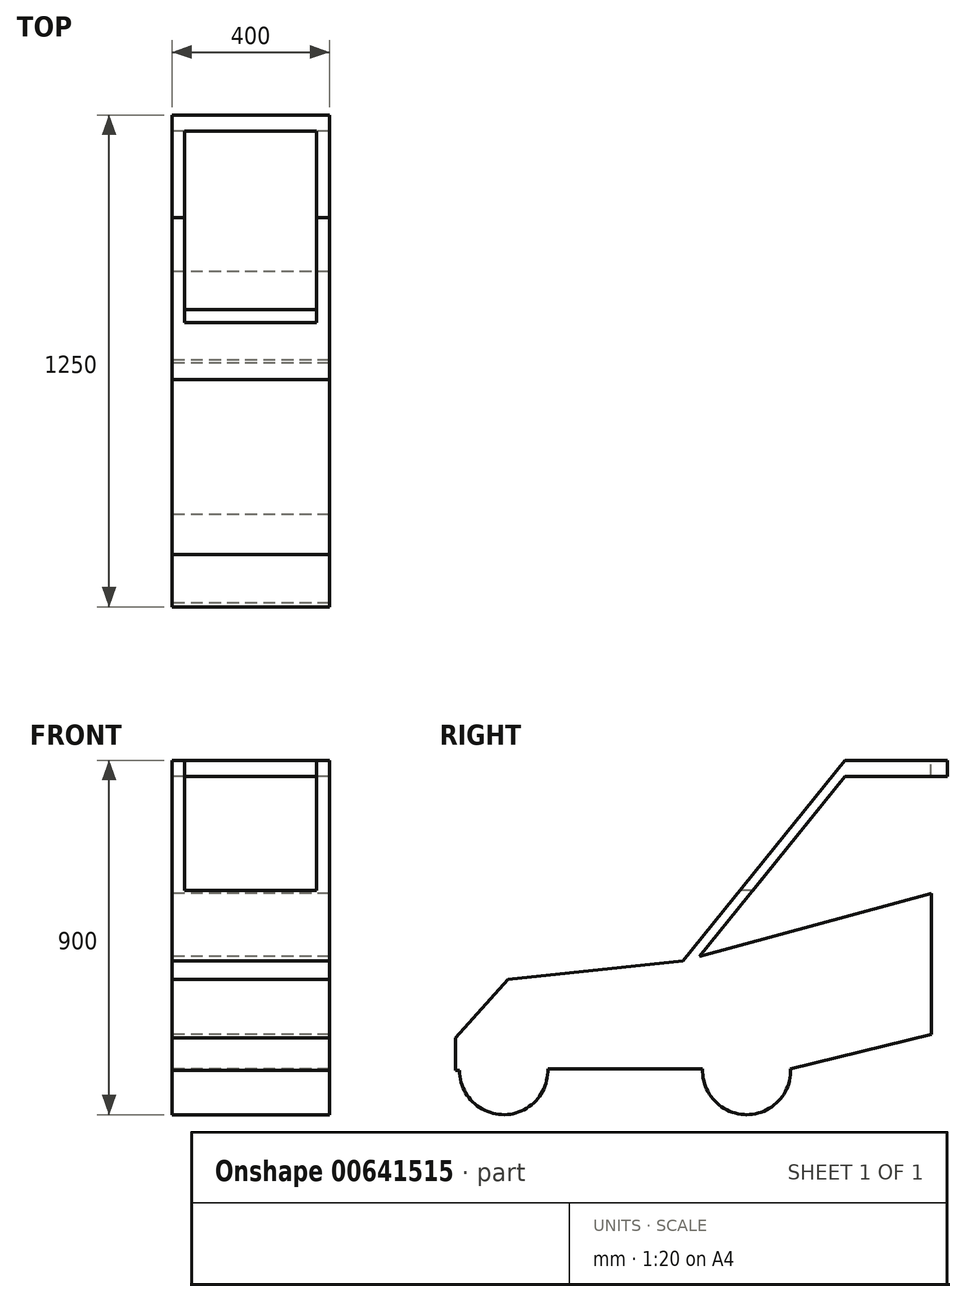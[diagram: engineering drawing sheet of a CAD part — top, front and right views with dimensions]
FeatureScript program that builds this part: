
annotation { "Feature Type Name" : "Feature", "Feature Type Description" : "" }
export const myFeature = defineFeature(function(context is Context, id is Id, definition is map)
    precondition{}
    {
        {
            var Q0;
            Q0=qCreatedBy(makeId("Right.planeOp"),FACE);
            var sketch = newSketch(context, id + "F0", { "sketchPlane" : qUnion([Q0])});
            skLineSegment(sketch, "E0.bottom", {"start": v(0, 0) * mm, "end": v(1250, 0) * mm, "construction": true});
            skLineSegment(sketch, "E0.top", {"start": v(0, 900) * mm, "end": v(1250, 900) * mm, "construction": true});
            skLineSegment(sketch, "E0.left", {"start": v(0, 0) * mm, "end": v(0, 900) * mm, "construction": true});
            skLineSegment(sketch, "E0.right", {"start": v(1250, 0) * mm, "end": v(1250, 900) * mm, "construction": true});
            skCircle(sketch, "E1", {"center": v(122.52, 111.92) * mm, "radius": 111.92 * mm});
            skCircle(sketch, "E2", {"center": v(739.64, 111.92) * mm, "radius": 111.92 * mm});
            skLineSegment(sketch, "E3", {"start": v(234.35, 116.4) * mm, "end": v(627.81, 116.4) * mm});
            skLineSegment(sketch, "E4", {"start": v(627.81, 116.4) * mm, "end": v(851.48, 116.4) * mm});
            skLineSegment(sketch, "E5", {"start": v(851.48, 116.4) * mm, "end": v(1208.92, 204.15) * mm});
            skLineSegment(sketch, "E6", {"start": v(1208.92, 204.15) * mm, "end": v(1208.92, 562.7) * mm});
            skLineSegment(sketch, "E7", {"start": v(1208.92, 562.7) * mm, "end": v(578.24, 391.02) * mm});
            skLineSegment(sketch, "E8", {"start": v(578.24, 391.02) * mm, "end": v(133.26, 343.13) * mm});
            skLineSegment(sketch, "E9", {"start": v(133.26, 343.13) * mm, "end": v(0, 194.8) * mm});
            skLineSegment(sketch, "E10", {"start": v(0, 194.8) * mm, "end": v(0, 111.92) * mm});
            skLineSegment(sketch, "E11", {"start": v(0, 111.92) * mm, "end": v(234.35, 116.4) * mm});
            skLineSegment(sketch, "E12", {"start": v(578.24, 391.02) * mm, "end": v(988.87, 900) * mm});
            skLineSegment(sketch, "E13", {"start": v(988.87, 900) * mm, "end": v(1250, 900) * mm});
            skLineSegment(sketch, "E14", {"start": v(1250, 859.42) * mm, "end": v(988.87, 859.42) * mm});
            skLineSegment(sketch, "E15", {"start": v(988.87, 859.42) * mm, "end": v(620.2, 402.44) * mm});
            skLineSegment(sketch, "E16", {"start": v(1250, 900) * mm, "end": v(1250, 859.42) * mm});
            skSolve(sketch);
        }
        {
            var Q0;
            {var subQ0=sQuery(id+"F0.wireOp",EDGE,"E4");Q0=makeQuery(id+"F0.imprint","IMPRINT",FACE,{"disambiguationData":[TD([[makeQuery(id+"F0.imprint","IMPRINT",EDGE,{"derivedFrom":subQ0}),1.0]])]});}
            var Q1;
            {var subQ0=sQuery(id+"F0.wireOp",EDGE,"E11");var subQ1=sQuery(id+"F0.wireOp",EDGE,"E1");var subQ3=makeQuery(id+"F0.imprint","INTERSECT",VERTEX,{"derivedFrom":[subQ1,subQ0]});Q1=makeQuery(id+"F0.imprint","IMPRINT",FACE,{"disambiguationData":[TD([[makeQuery(id+"F0.imprint","IMPRINT",EDGE,{"disambiguationData":[TD([[subQ3,-1.0]])],"derivedFrom":subQ1}),1.0]])]});}
            var Q2;
            {var subQ0=sQuery(id+"F0.wireOp",EDGE,"E11");var subQ1=sQuery(id+"F0.wireOp",EDGE,"E1");var subQ3=makeQuery(id+"F0.imprint","INTERSECT",VERTEX,{"derivedFrom":[subQ1,subQ0]});Q2=makeQuery(id+"F0.imprint","IMPRINT",FACE,{"disambiguationData":[TD([[makeQuery(id+"F0.imprint","IMPRINT",EDGE,{"disambiguationData":[TD([[subQ3,1.0]])],"derivedFrom":subQ1}),1.0]])]});}
            var Q3;
            {var subQ0=sQuery(id+"F0.wireOp",EDGE,"E4");Q3=makeQuery(id+"F0.imprint","IMPRINT",FACE,{"disambiguationData":[TD([[makeQuery(id+"F0.imprint","IMPRINT",EDGE,{"derivedFrom":subQ0}),-1.0]])]});}
            var Q4;
            {var subQ6=sQuery(id+"F0.wireOp",EDGE,"E3");Q4=makeQuery(id+"F0.imprint","IMPRINT",FACE,{"disambiguationData":[TD([[makeQuery(id+"F0.imprint","IMPRINT",EDGE,{"derivedFrom":subQ6}),1.0]])]});}
            var Q5;
            {var subQ0=sQuery(id+"F0.wireOp",EDGE,"E12");Q5=makeQuery(id+"F0.imprint","IMPRINT",FACE,{"disambiguationData":[TD([[makeQuery(id+"F0.imprint","IMPRINT",EDGE,{"derivedFrom":subQ0}),-1.0]])]});}
            extrude(context, id + "F1", {"entities" : qUnion([Q0, Q1, Q2, Q3, Q4, Q5]), "endBound" : BoundingType.SYMMETRIC, "depth" : 400 * mm, "offsetDistance" : 25 * mm});
        }
        {
            var Q0;
            Q0=makeQuery(id+"F1.opExtrude","SWEPT_FACE",FACE,{"disambiguationData":[OSD([sQuery(id+"F0.wireOp",EDGE,"E13")])]});
            var sketch = newSketch(context, id + "F2", { "sketchPlane" : qUnion([Q0])});
            skLineSegment(sketch, "E17.bottom", {"start": v(-168.35, 1208.4) * mm, "end": v(166.7, 1208.4) * mm});
            skLineSegment(sketch, "E17.top", {"start": v(-168.35, 508.63) * mm, "end": v(166.7, 508.63) * mm});
            skLineSegment(sketch, "E17.left", {"start": v(-168.35, 1208.4) * mm, "end": v(-168.35, 508.63) * mm});
            skLineSegment(sketch, "E17.right", {"start": v(166.7, 1208.4) * mm, "end": v(166.7, 508.63) * mm});
            skSolve(sketch);
        }
        {
            var Q0;
            Q0 = qSketchRegion(id + "F2", true);
            extrude(context, id + "F3", {"entities" : qUnion([Q0]), "operationType" : NewBodyOperationType.REMOVE, "oppositeDirection" : true, "depth" : 330.22 * mm, "offsetDistance" : 25 * mm});
        }
    });
